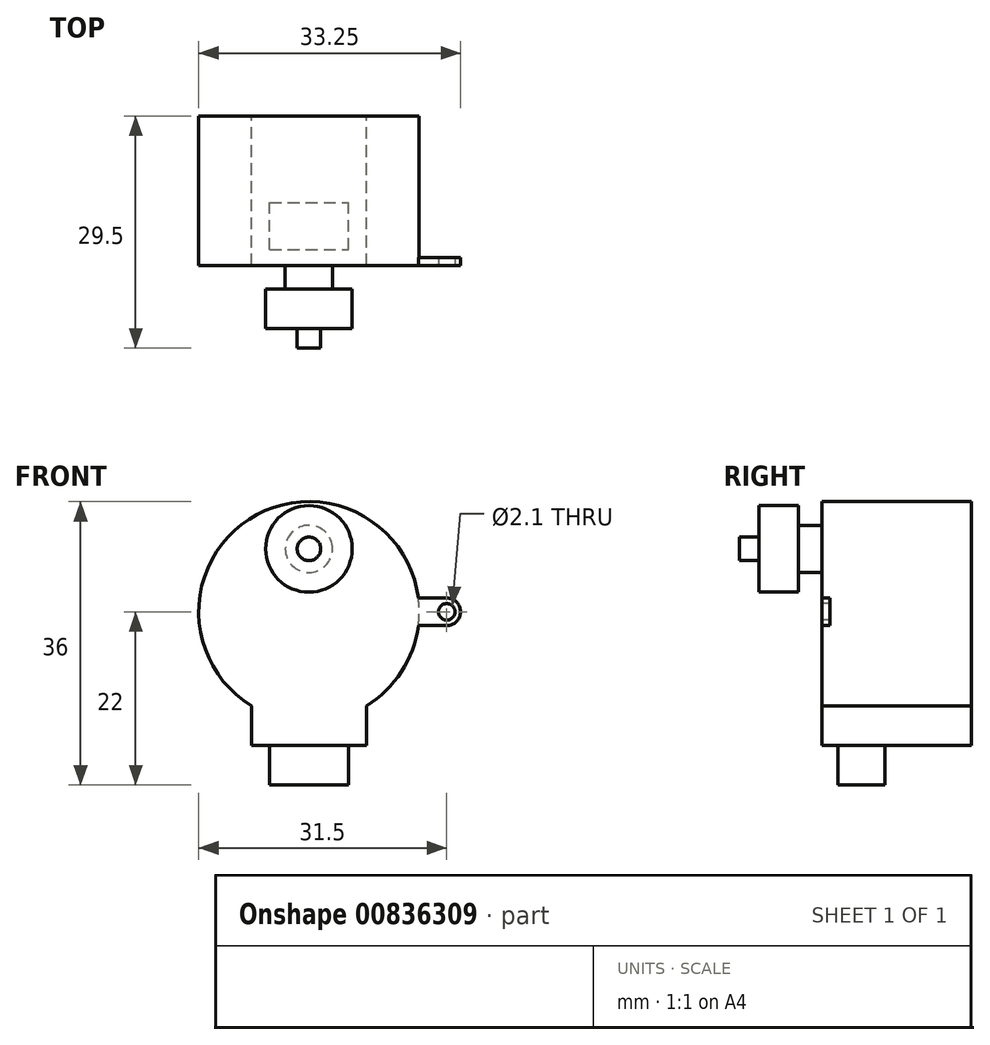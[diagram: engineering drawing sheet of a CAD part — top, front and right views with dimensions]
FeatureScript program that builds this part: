
annotation { "Feature Type Name" : "Feature", "Feature Type Description" : "" }
export const myFeature = defineFeature(function(context is Context, id is Id, definition is map)
    precondition{}
    {
        {
            var Q0;
            Q0=qCreatedBy(makeId("Front.planeOp"),FACE);
            var sketch = newSketch(context, id + "F0", { "sketchPlane" : qUnion([Q0])});
            skArc(sketch, "E0", {"start": v(7.3, -11.95) * mm, "mid": v(0, 14) * mm, "end": v(-7.3, -11.95) * mm});
            skLineSegment(sketch, "E1.top", {"start": v(-7.3, -17) * mm, "end": v(7.3, -17) * mm});
            skLineSegment(sketch, "E1.left", {"start": v(-7.3, -11.95) * mm, "end": v(-7.3, -17) * mm});
            skLineSegment(sketch, "E1.right", {"start": v(7.3, -11.95) * mm, "end": v(7.3, -17) * mm});
            skLineSegment(sketch, "E2", {"start": v(0, 0) * mm, "end": v(0, -8.8) * mm, "construction": true});
            skSolve(sketch);
        }
        {
            var Q0;
            Q0=qSketchRegion(id+"F0",true);
            extrude(context, id + "F1", {"entities" : qUnion([Q0]), "depth" : 19 * mm, "offsetDistance" : 25 * mm});
        }
        {
            var Q0;
            Q0=makeQuery(id+"F1.opExtrude","CAP_FACE",FACE,{"disambiguationData":[OSD([sQuery(id+"F0.wireOp",EDGE,"E0"),sQuery(id+"F0.wireOp",EDGE,"E1.top"),sQuery(id+"F0.wireOp",EDGE,"E1.left"),sQuery(id+"F0.wireOp",EDGE,"E1.right")])],"isStart":false});
            var sketch = newSketch(context, id + "F2", { "sketchPlane" : qUnion([Q0])});
            skCircle(sketch, "E3", {"center": v(0, 8) * mm, "radius": 3 * mm});
            skSolve(sketch);
        }
        {
            var Q0;
            Q0=qSketchRegion(id+"F2",true);
            extrude(context, id + "F3", {"entities" : qUnion([Q0]), "operationType" : NewBodyOperationType.ADD, "depth" : 3 * mm, "offsetDistance" : 25 * mm});
        }
        {
            var Q0;
            Q0=makeQuery(id+"F3.opExtrude","CAP_FACE",FACE,{"disambiguationData":[OSD([sQuery(id+"F2.wireOp",EDGE,"E3")])],"isStart":false});
            var sketch = newSketch(context, id + "F4", { "sketchPlane" : qUnion([Q0])});
            skCircle(sketch, "E4", {"center": v(0, 8) * mm, "radius": 1.5 * mm});
            skSolve(sketch);
        }
        {
            var Q0;
            Q0=qSketchRegion(id+"F4",true);
            extrude(context, id + "F5", {"entities" : qUnion([Q0]), "operationType" : NewBodyOperationType.ADD, "depth" : 7.5 * mm, "offsetDistance" : 25 * mm});
        }
        {
            var Q0;
            Q0=makeQuery(id+"F1.opExtrude","CAP_FACE",FACE,{"disambiguationData":[OSD([sQuery(id+"F0.wireOp",EDGE,"E0"),sQuery(id+"F0.wireOp",EDGE,"E1.top"),sQuery(id+"F0.wireOp",EDGE,"E1.left"),sQuery(id+"F0.wireOp",EDGE,"E1.right")])],"isStart":false});
            var sketch = newSketch(context, id + "F6", { "sketchPlane" : qUnion([Q0])});
            skCircle(sketch, "E5", {"center": v(17.5, 0) * mm, "radius": 1.05 * mm});
            skArc(sketch, "E6", {"start": v(17.5, -1.75) * mm, "mid": v(19.25, 0) * mm, "end": v(17.5, 1.75) * mm});
            skLineSegment(sketch, "E7", {"start": v(17.5, 1.75) * mm, "end": v(13.9, 1.75) * mm});
            skLineSegment(sketch, "E8", {"start": v(17.5, -1.75) * mm, "end": v(13.9, -1.75) * mm});
            skLineSegment(sketch, "E9", {"start": v(13.9, 1.75) * mm, "end": v(13.9, -1.75) * mm});
            skSolve(sketch);
        }
        {
            var Q0;
            Q0=qSketchRegion(id+"F6",true);
            extrude(context, id + "F7", {"entities" : qUnion([Q0]), "operationType" : NewBodyOperationType.ADD, "oppositeDirection" : true, "depth" : 1 * mm, "offsetDistance" : 25 * mm});
        }
        {
            var Q0;
            Q0=makeQuery(id+"F3.opExtrude","CAP_FACE",FACE,{"disambiguationData":[OSD([sQuery(id+"F2.wireOp",EDGE,"E3")])],"isStart":false});
            var sketch = newSketch(context, id + "F8", { "sketchPlane" : qUnion([Q0])});
            skCircle(sketch, "E10", {"center": v(0, 8) * mm, "radius": 5.5 * mm});
            skSolve(sketch);
        }
        {
            var Q0;
            Q0=qSketchRegion(id+"F8",true);
            extrude(context, id + "F9", {"entities" : qUnion([Q0]), "operationType" : NewBodyOperationType.ADD, "depth" : 5 * mm, "offsetDistance" : 25 * mm});
        }
        {
            var Q0;
            Q0=makeQuery(id+"F1.opExtrude","SWEPT_FACE",FACE,{"disambiguationData":[OSD([sQuery(id+"F0.wireOp",EDGE,"E1.top")])]});
            var sketch = newSketch(context, id + "F10", { "sketchPlane" : qUnion([Q0])});
            skLineSegment(sketch, "E11.bottom", {"start": v(-5, 17) * mm, "end": v(5, 17) * mm});
            skLineSegment(sketch, "E11.top", {"start": v(-5, 11) * mm, "end": v(5, 11) * mm});
            skLineSegment(sketch, "E11.left", {"start": v(-5, 17) * mm, "end": v(-5, 11) * mm});
            skLineSegment(sketch, "E11.right", {"start": v(5, 17) * mm, "end": v(5, 11) * mm});
            skPoint(sketch, "E12", {"position": v(0, 19) * mm});
            skPoint(sketch, "E13", {"position": v(0, 17) * mm});
            skSolve(sketch);
        }
        {
            var Q0;
            Q0=qSketchRegion(id+"F10",true);
            extrude(context, id + "F11", {"entities" : qUnion([Q0]), "operationType" : NewBodyOperationType.ADD, "depth" : 5 * mm, "offsetDistance" : 25 * mm});
        }
    });
